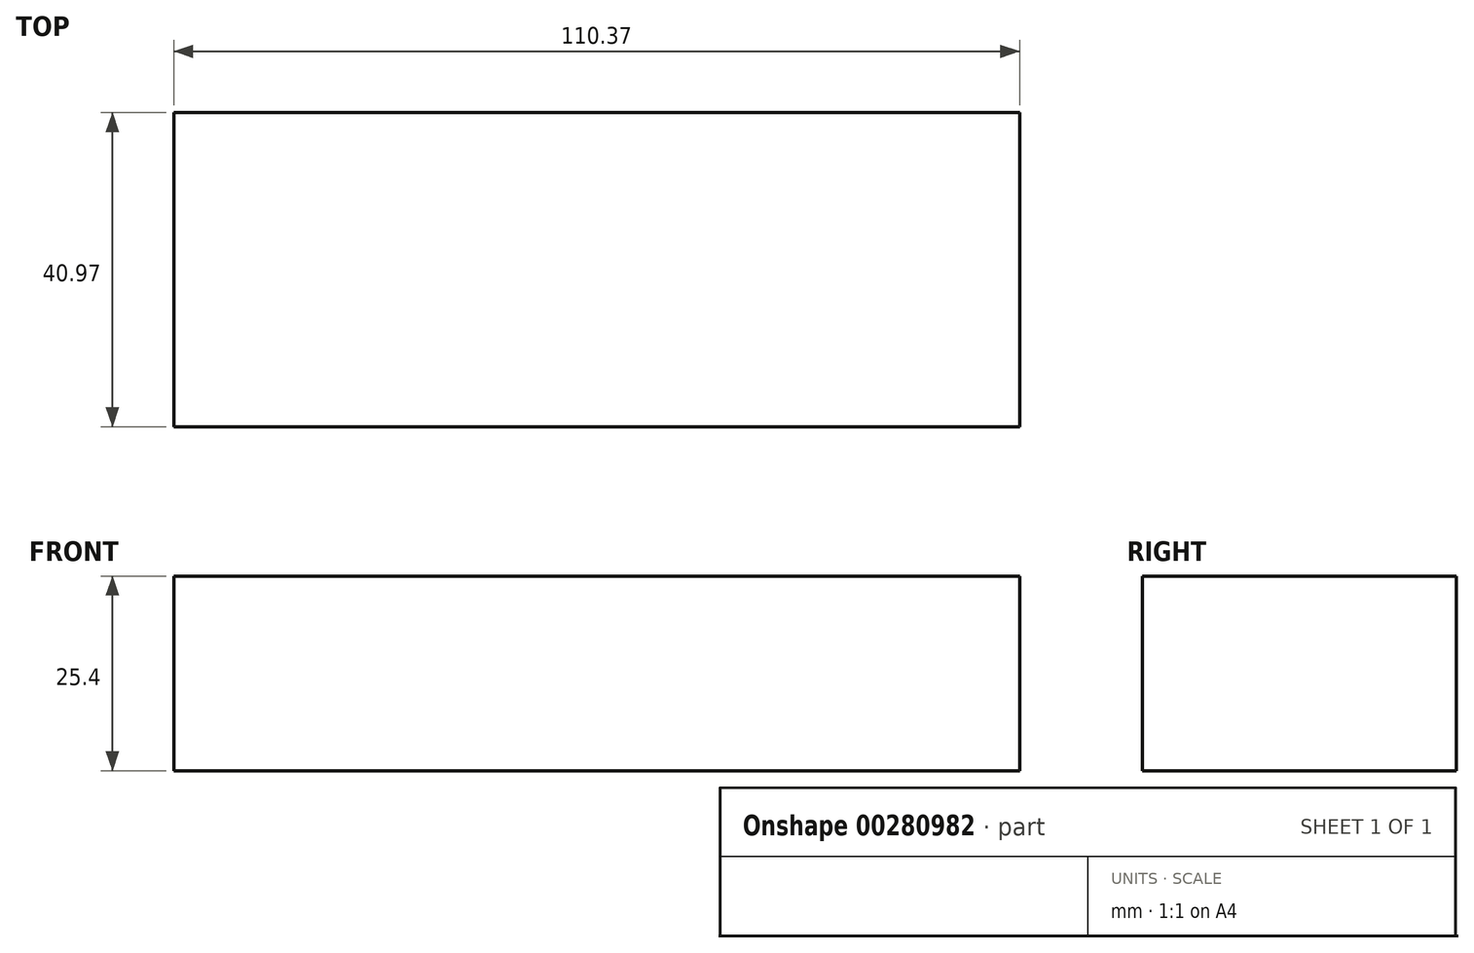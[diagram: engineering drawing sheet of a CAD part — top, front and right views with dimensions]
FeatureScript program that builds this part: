
annotation { "Feature Type Name" : "Feature", "Feature Type Description" : "" }
export const myFeature = defineFeature(function(context is Context, id is Id, definition is map)
    precondition{}
    {
        {
            var Q0;
            Q0=qCreatedBy(makeId("Top.planeOp"),FACE);
            var sketch = newSketch(context, id + "F0", { "sketchPlane" : qUnion([Q0])});
            skLineSegment(sketch, "E0.bottom", {"start": v(-71.57, -26.67) * mm, "end": v(38.8, -26.67) * mm});
            skLineSegment(sketch, "E0.top", {"start": v(-71.57, -67.64) * mm, "end": v(38.8, -67.64) * mm});
            skLineSegment(sketch, "E0.left", {"start": v(-71.57, -26.67) * mm, "end": v(-71.57, -67.64) * mm});
            skLineSegment(sketch, "E0.right", {"start": v(38.8, -26.67) * mm, "end": v(38.8, -67.64) * mm});
            skSolve(sketch);
        }
        {
            var Q0;
            Q0 = qSketchRegion(id + "F0", true);
            extrude(context, id + "F1", {"entities" : qUnion([Q0]), "depth" : 25.4 * mm});
        }
    });
